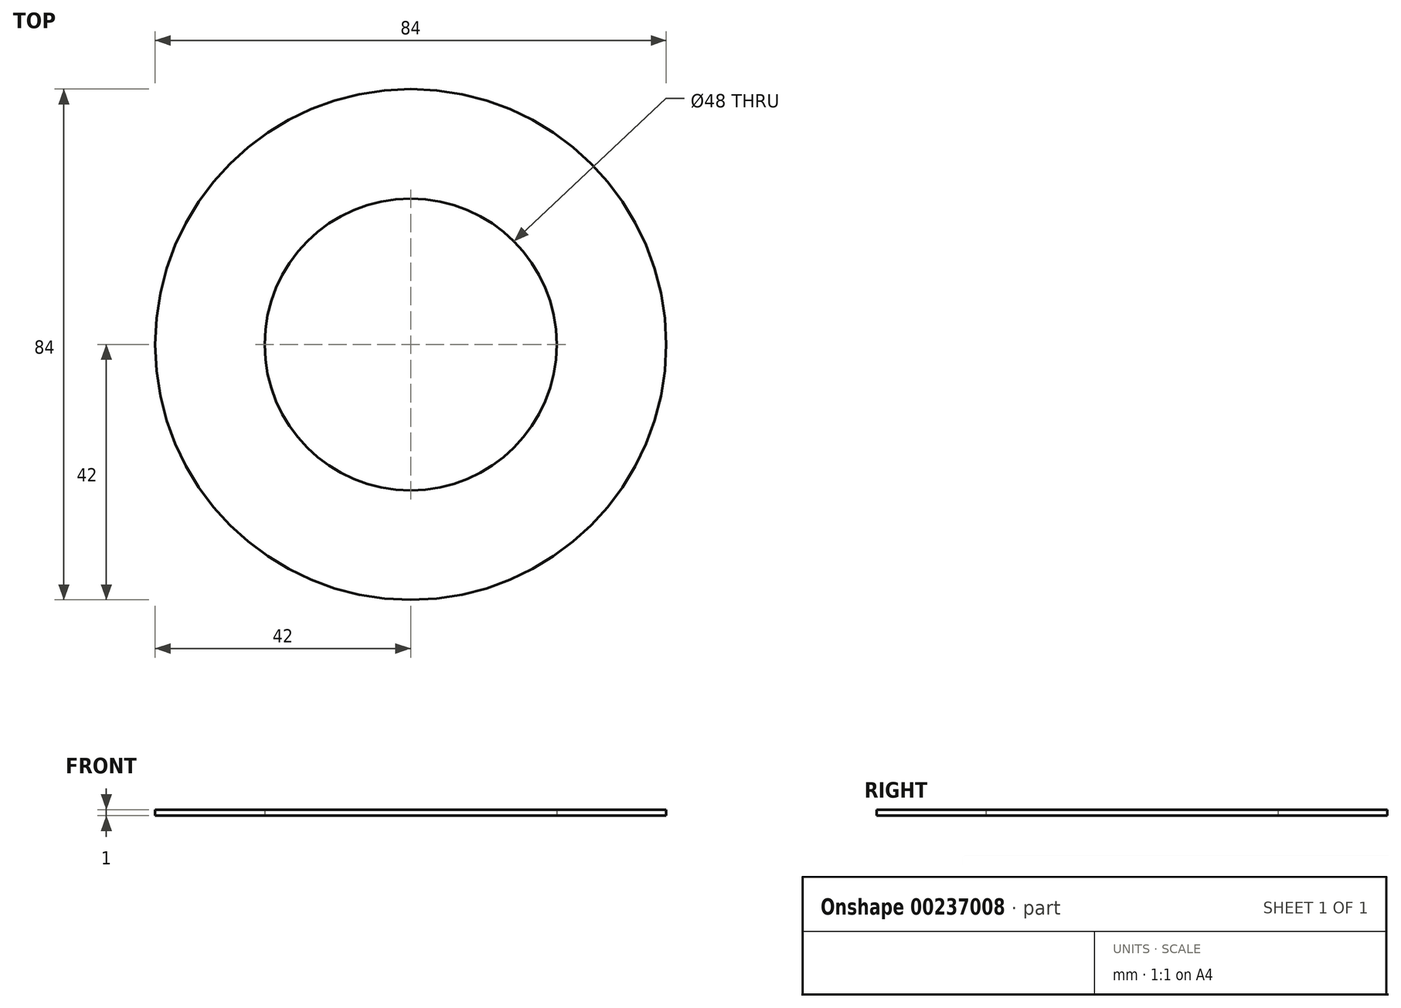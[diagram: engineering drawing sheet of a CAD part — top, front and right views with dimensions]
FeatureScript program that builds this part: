
annotation { "Feature Type Name" : "Feature", "Feature Type Description" : "" }
export const myFeature = defineFeature(function(context is Context, id is Id, definition is map)
    precondition{}
    {
        {
            var Q0;
            Q0=qCreatedBy(makeId("Top.planeOp"),FACE);
            var sketch = newSketch(context, id + "F0", { "sketchPlane" : qUnion([Q0])});
            skCircle(sketch, "E0", {"center": v(0, 0) * mm, "radius": 24 * mm});
            skCircle(sketch, "E1", {"center": v(0, 0) * mm, "radius": 42 * mm});
            skSolve(sketch);
        }
        {
            var Q0;
            Q0 = qSketchRegion(id + "F0", true);
            extrude(context, id + "F1", {"entities" : qUnion([Q0]), "depth" : 1 * mm});
        }
    });
